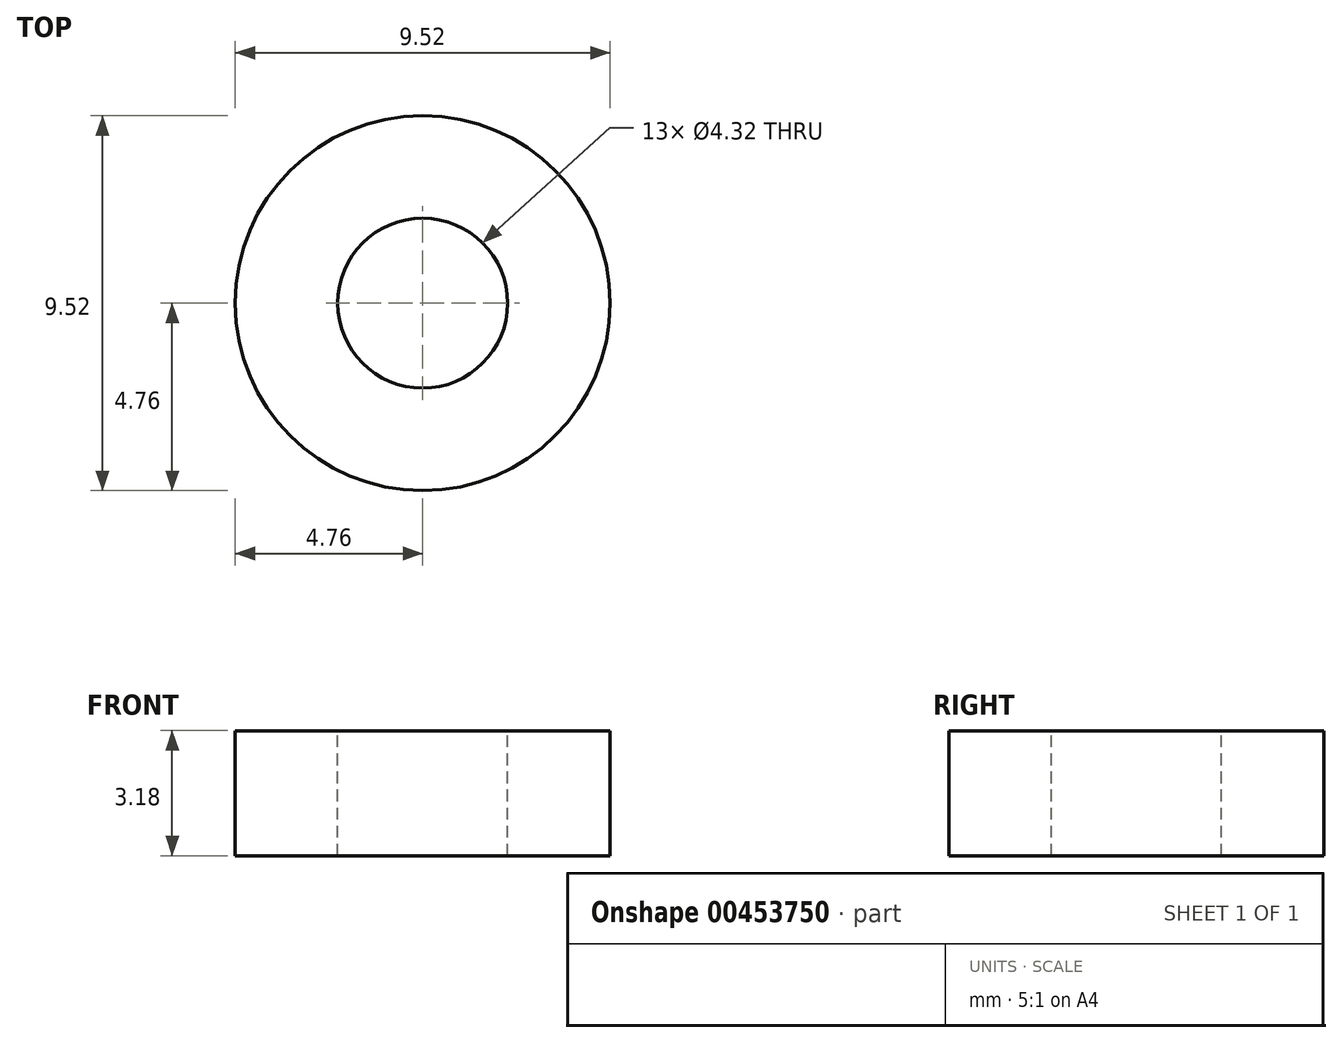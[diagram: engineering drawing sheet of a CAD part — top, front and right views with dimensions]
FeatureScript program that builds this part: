
annotation { "Feature Type Name" : "Feature", "Feature Type Description" : "" }
export const myFeature = defineFeature(function(context is Context, id is Id, definition is map)
    precondition{}
    {
        {
            var Q0;
            Q0=qCreatedBy(makeId("Top.planeOp"),FACE);
            var sketch = newSketch(context, id + "F0", { "sketchPlane" : qUnion([Q0])});
            skCircle(sketch, "E0", {"center": v(0, 0) * mm, "radius": 4.76 * mm});
            skSolve(sketch);
        }
        {
            var Q0;
            Q0=makeQuery(id+"F0.imprint","IMPRINT",FACE,{"disambiguationData":[TD([[makeQuery(id+"F0.imprint","IMPRINT",EDGE,{"derivedFrom":sQuery(id+"F0.wireOp",EDGE,"E0")}),1.0]])]});
            extrude(context, id + "F1", {"entities" : qUnion([Q0]), "depth" : 3.17 * mm});
        }
        {
            var Q0;
            Q0=makeQuery(id+"F1.opExtrude","CAP_FACE",FACE,{"disambiguationData":[OSD([sQuery(id+"F0.wireOp",EDGE,"E0")])],"isStart":false});
            var sketch = newSketch(context, id + "F2", { "sketchPlane" : qUnion([Q0])});
            skCircle(sketch, "E1", {"center": v(0, 0) * mm, "radius": 2.16 * mm});
            skSolve(sketch);
        }
        {
            var Q0;
            Q0=makeQuery(id+"F2.imprint","IMPRINT",FACE,{"disambiguationData":[TD([[makeQuery(id+"F2.imprint","IMPRINT",EDGE,{"derivedFrom":sQuery(id+"F2.wireOp",EDGE,"E1")}),1.0]])]});
            var Q1;
            Q1=sQuery(id+"F2.wireOp",EDGE,"E1");
            extrude(context, id + "F3", {"entities" : qUnion([Q0]), "operationType" : NewBodyOperationType.REMOVE, "surfaceEntities" : qUnion([Q1]), "endBound" : BoundingType.THROUGH_ALL, "oppositeDirection" : true, "depth" : 25.4 * mm});
        }
    });
